# Revit family: PRD_FrankeWS_ThrmsticMxngVlvs_ThermostaticMixingValve_PURE0031
name_source: partatom
category: Pipe Accessories
revit_build: Autodesk Revit 2018 (Build: 20190510_1515(x64)
units: mm (PartAtom-declared; Revit-internal decimal feet)

## family parameters
Always vertical = No
Cut with Voids When Loaded = No
OmniClass Number = 23.65.55.14.24
OmniClass Title = Mixing Valves for Liquid Services
Part Type = Valve - Breaks Into
Round Connector Dimension = Use Diameter
Shared = No
Work Plane-Based = No

## types (1)
- PURE0031
    AssetType = Fixed
    BIMObjectName = PRD_AR_ThermostaticMixingValves_PURE0031
    Category = Pr_65_54_95_88, Thermostatic mixing valves
    CloseOffRating = 0.0 Pa
    Connections = 20.000 mm
    Description = PURETHERM thermostatic mixing valve, DN 10 to be used as anti-scalding protection safety device for washbasin taps in case cold water supply fails. Outlets G 3/8 B and union nut G 3/8 for connection to the elbow valve underneath washbasins. With facilities for performing manual thermal disinfection. Installation kit for PURETHERM thermostatic mixing valve has to be ordered separately.
    DurationUnit = year
    FlowCoefficient = 0
    GrossWeight = 0.75 kg
    IfcExportAs = IfcValveType
    IfcExportType = NOTDEFINED
    InletSize = 10.000 mm
    Manufacturer = KWC Group AG
    ManufacturerName = KWC Group AG
    ManufacturerURL = www.kwc.com
    Model = PURE0031
    ModelNumber = 2030012758
    ModelReference = PURE0031
    NBSDescription = Thermostatic mixing valves
    NBSReference = 90-10-90/370
    Name = Thermostatic mixing valve PURE0031
    NetWeight = 0.71 kg
    NominalHeight = 0 mm  [stored 0 ft]
    NominalLength = 0 mm  [stored 0 ft]
    NominalWidth = 0 mm  [stored 0 ft]
    OutletSize = 10.000 mm
    ProductInformation = https://pim.kwc.com
    Size = DN10, 3-8inch
    TestPressure = 0.0 Pa
    URL = www.kwc.com
    Uniclass2015Code = Pr_65_54_95_88
    Uniclass2015Title = Thermostatic mixing valves
    Uniclass2015Version = Products v1.7
    ValveMaterial = PRD_AR_StainlessSteel_SatinFinished
    ValveMechanism = Other
    ValveOperation = Other
    ValvePattern = STRAIGHT_2_PORT
    Version = 1
    WarrantyDurationUnit = year

note: [stored X ft] marks values corroborated as IEEE doubles in the binary element streams (Revit-internal decimal feet)

## geometry (parser evidence)
native form markers: Sweep x2
no freeform markers — native parametric forms only
